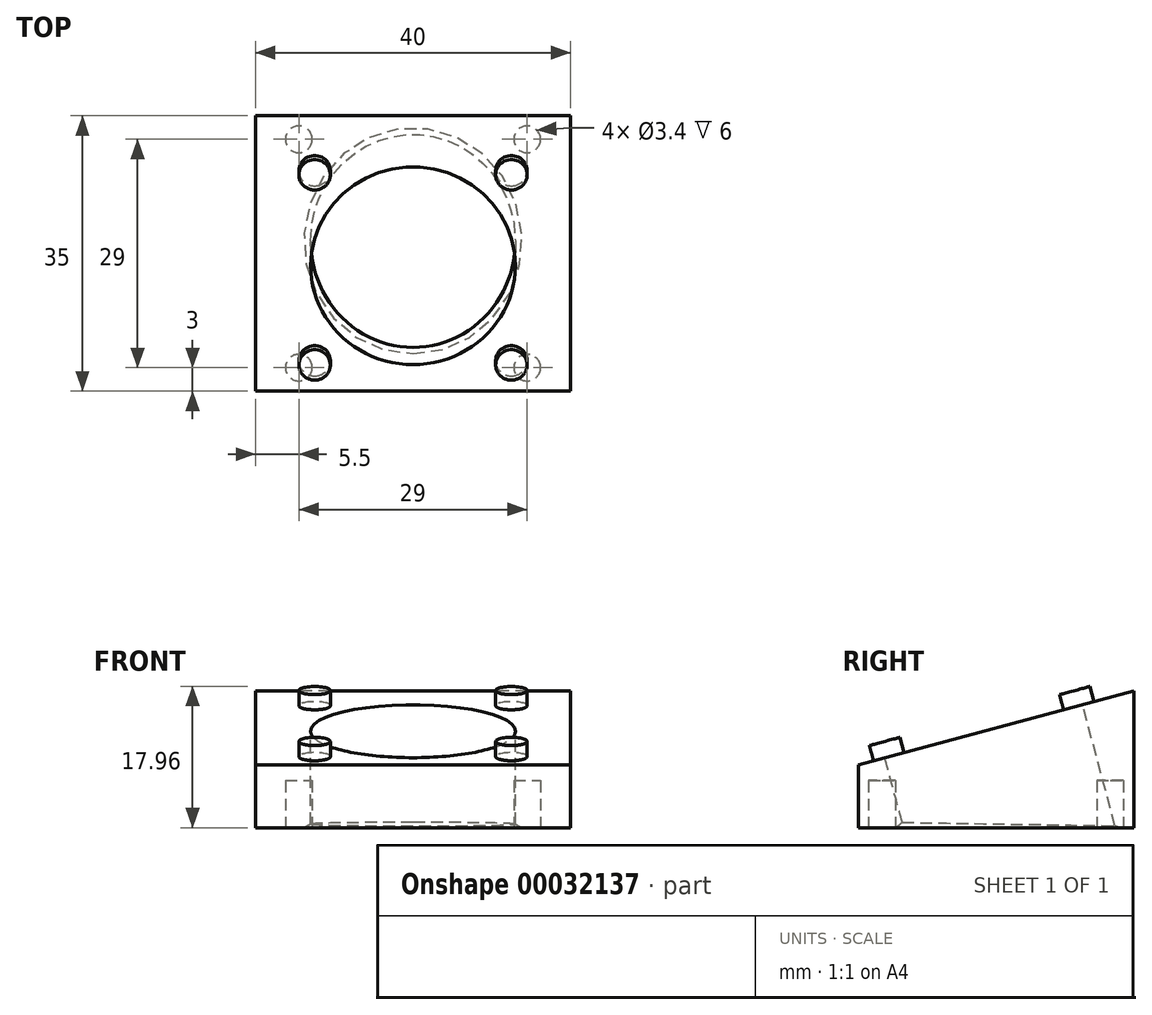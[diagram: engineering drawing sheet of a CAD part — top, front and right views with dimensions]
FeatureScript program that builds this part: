
annotation { "Feature Type Name" : "Feature", "Feature Type Description" : "" }
export const myFeature = defineFeature(function(context is Context, id is Id, definition is map)
    precondition{}
    {
        {
            var Q0;
            Q0=qCreatedBy(makeId("Right.planeOp"),FACE);
            var sketch = newSketch(context, id + "F0", { "sketchPlane" : qUnion([Q0])});
            skLineSegment(sketch, "E0.bottom", {"start": v(0, 0) * mm, "end": v(35, 0) * mm});
            skLineSegment(sketch, "E0.top", {"start": v(0, 8) * mm, "end": v(35, 8) * mm, "construction": true});
            skLineSegment(sketch, "E0.left", {"start": v(0, 0) * mm, "end": v(0, 8) * mm});
            skLineSegment(sketch, "E0.right", {"start": v(35, 0) * mm, "end": v(35, 8) * mm});
            skLineSegment(sketch, "E1", {"start": v(0, 8) * mm, "end": v(35, 17.38) * mm});
            skLineSegment(sketch, "E2", {"start": v(35, 17.38) * mm, "end": v(35, 8) * mm});
            skSolve(sketch);
        }
        {
            var Q0;
            Q0 = qSketchRegion(id + "F0", true);
            extrude(context, id + "F1", {"entities" : qUnion([Q0]), "endBound" : BoundingType.SYMMETRIC, "depth" : 40 * mm});
        }
        {
            var Q0;
            Q0=makeQuery(id+"F1.opExtrude","SWEPT_FACE",FACE,{"disambiguationData":[OSD([sQuery(id+"F0.wireOp",EDGE,"E1")])]});
            var sketch = newSketch(context, id + "F2", { "sketchPlane" : qUnion([Q0])});
            skCircle(sketch, "E3", {"center": v(0, 18.57) * mm, "radius": 13 * mm});
            skSolve(sketch);
        }
        {
            var Q0;
            Q0 = qSketchRegion(id + "F2", true);
            extrude(context, id + "F3", {"entities" : qUnion([Q0]), "operationType" : NewBodyOperationType.REMOVE, "endBound" : BoundingType.THROUGH_ALL, "oppositeDirection" : true, "depth" : 25 * mm});
        }
        {
            var Q0;
            Q0=makeQuery(id+"F1.opExtrude","SWEPT_FACE",FACE,{"disambiguationData":[OSD([sQuery(id+"F0.wireOp",EDGE,"E1")])]});
            var sketch = newSketch(context, id + "F4", { "sketchPlane" : qUnion([Q0])});
            skLineSegment(sketch, "E4.rect.bottom", {"start": v(12.5, 31.07) * mm, "end": v(-12.5, 31.07) * mm, "construction": true});
            skLineSegment(sketch, "E4.rect.top", {"start": v(12.5, 6.07) * mm, "end": v(-12.5, 6.07) * mm, "construction": true});
            skLineSegment(sketch, "E4.rect.left", {"start": v(12.5, 31.07) * mm, "end": v(12.5, 6.07) * mm, "construction": true});
            skLineSegment(sketch, "E4.rect.right", {"start": v(-12.5, 31.07) * mm, "end": v(-12.5, 6.07) * mm, "construction": true});
            skPoint(sketch, "E4.rect.middle", {"position": v(0, 18.57) * mm});
            skCircle(sketch, "E5", {"center": v(12.5, 31.07) * mm, "radius": 2 * mm});
            skCircle(sketch, "E6", {"center": v(-12.5, 31.07) * mm, "radius": 2 * mm});
            skCircle(sketch, "E7", {"center": v(-12.5, 6.07) * mm, "radius": 2 * mm});
            skCircle(sketch, "E8", {"center": v(12.5, 6.07) * mm, "radius": 2 * mm});
            skSolve(sketch);
        }
        {
            var Q0;
            Q0 = qSketchRegion(id + "F4", true);
            extrude(context, id + "F5", {"entities" : qUnion([Q0]), "operationType" : NewBodyOperationType.ADD, "depth" : 2 * mm});
        }
        {
            var Q0;
            Q0=makeQuery(id+"F1.opExtrude","SWEPT_FACE",FACE,{"disambiguationData":[OSD([sQuery(id+"F0.wireOp",EDGE,"E0.bottom")])]});
            var sketch = newSketch(context, id + "F6", { "sketchPlane" : qUnion([Q0])});
            skLineSegment(sketch, "E9.rect.bottom", {"start": v(14.5, -3) * mm, "end": v(-14.5, -3) * mm, "construction": true});
            skLineSegment(sketch, "E9.rect.top", {"start": v(14.5, -32) * mm, "end": v(-14.5, -32) * mm, "construction": true});
            skLineSegment(sketch, "E9.rect.left", {"start": v(14.5, -3) * mm, "end": v(14.5, -32) * mm, "construction": true});
            skLineSegment(sketch, "E9.rect.right", {"start": v(-14.5, -3) * mm, "end": v(-14.5, -32) * mm, "construction": true});
            skPoint(sketch, "E9.rect.middle", {"position": v(0, -17.5) * mm});
            skCircle(sketch, "E10", {"center": v(-14.5, -3) * mm, "radius": 1.7 * mm});
            skCircle(sketch, "E11", {"center": v(14.5, -3) * mm, "radius": 1.7 * mm});
            skCircle(sketch, "E12", {"center": v(14.5, -32) * mm, "radius": 1.7 * mm});
            skCircle(sketch, "E13", {"center": v(-14.5, -32) * mm, "radius": 1.7 * mm});
            skSolve(sketch);
        }
        {
            var Q0;
            Q0 = qSketchRegion(id + "F6", true);
            extrude(context, id + "F7", {"entities" : qUnion([Q0]), "operationType" : NewBodyOperationType.REMOVE, "oppositeDirection" : true, "depth" : 6 * mm});
        }
        {
            var Q0;
            Q0=makeQuery(id+"F3.boolean.opBoolean","COPY",EDGE,{"derivedFrom":makeQuery(id+"F3.opExtrude","CAP_EDGE",EDGE,{"disambiguationData":[OSD([sQuery(id+"F2.wireOp",EDGE,"E3")])],"isStart":true})});
            var Q1;
            Q1=makeQuery(id+"F3.boolean.opBoolean","INTERSECT",EDGE,{"derivedFrom":[makeQuery(id+"F1.opExtrude","SWEPT_FACE",FACE,{"disambiguationData":[OSD([sQuery(id+"F0.wireOp",EDGE,"E0.bottom")])]}),makeQuery(id+"F3.opExtrude","SWEPT_FACE",FACE,{"disambiguationData":[OSD([sQuery(id+"F2.wireOp",EDGE,"E3")])]})]});
            chamfer(context, id + "F8", {"entities" : qUnion([Q0, Q1]), "chamferType" : ChamferType.OFFSET_ANGLE, "width" : 1 * mm, "oppositeDirection" : false, "angle" : 40 * degree, "tangentPropagation" : true});
        }
    });
